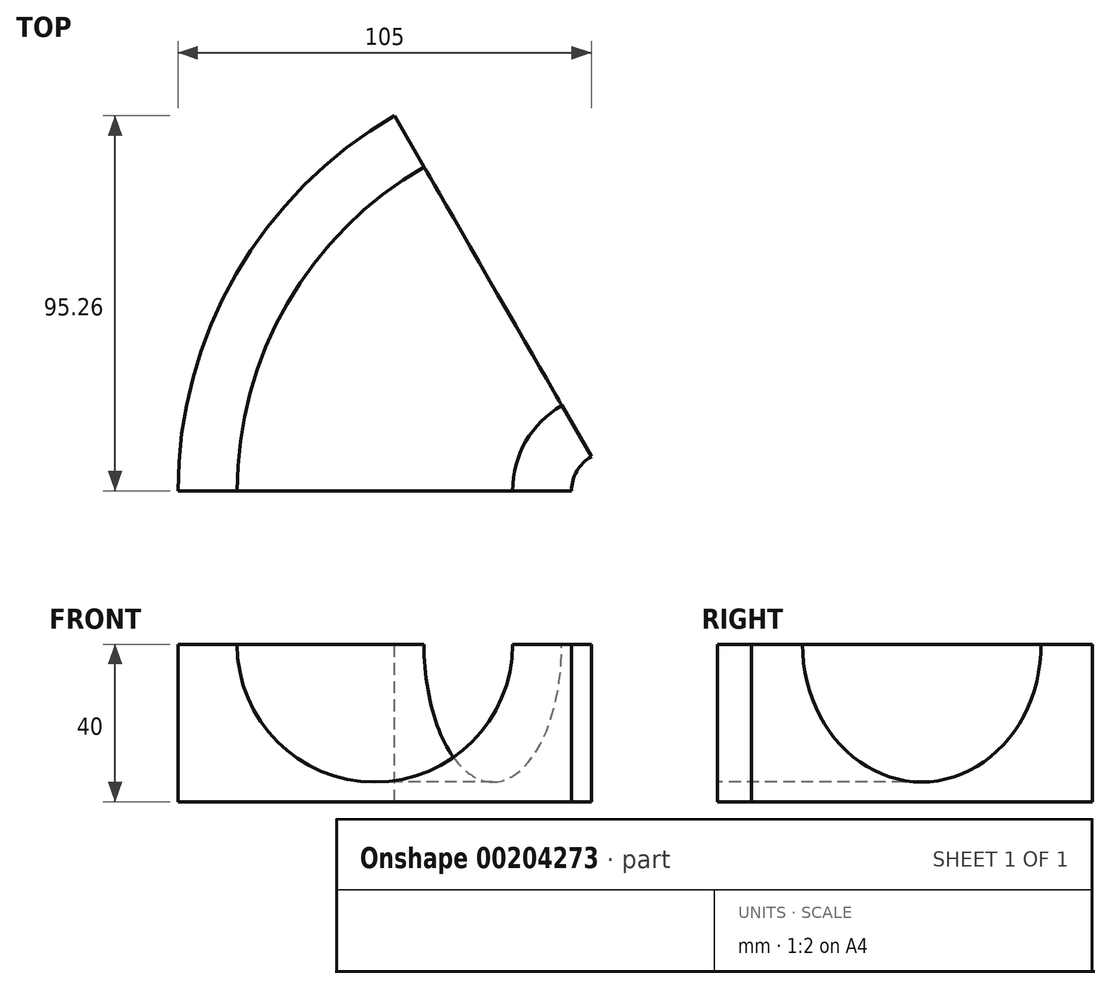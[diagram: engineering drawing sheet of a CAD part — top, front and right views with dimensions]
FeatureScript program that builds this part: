
annotation { "Feature Type Name" : "Feature", "Feature Type Description" : "" }
export const myFeature = defineFeature(function(context is Context, id is Id, definition is map)
    precondition{}
    {
        {
            var Q0;
            Q0=qCreatedBy(makeId("Front.planeOp"),FACE);
            var sketch = newSketch(context, id + "F0", { "sketchPlane" : qUnion([Q0])});
            skLineSegment(sketch, "E0.bottom", {"start": v(-50, -19.67) * mm, "end": v(0, -19.67) * mm});
            skLineSegment(sketch, "E0.top", {"start": v(-50, 20.33) * mm, "end": v(0, 20.33) * mm});
            skLineSegment(sketch, "E0.left", {"start": v(-50, -19.67) * mm, "end": v(-50, 20.33) * mm});
            skLineSegment(sketch, "E1.MirrorCS", {"start": v(50, -19.67) * mm, "end": v(0, -19.67) * mm});
            skLineSegment(sketch, "E2.MirrorCS", {"start": v(50, -19.67) * mm, "end": v(50, 20.33) * mm});
            skLineSegment(sketch, "E3.MirrorCS", {"start": v(50, 20.33) * mm, "end": v(0, 20.33) * mm});
            skArc(sketch, "E4", {"start": v(-35, 20.33) * mm, "mid": v(0, -14.67) * mm, "end": v(35, 20.33) * mm});
            skLineSegment(sketch, "E5", {"start": v(50, 20.33) * mm, "end": v(60, 20.33) * mm, "construction": true});
            skLineSegment(sketch, "E6", {"start": v(60, 20.33) * mm, "end": v(60, -18.07) * mm, "construction": true});
            skSolve(sketch);
        }
        {
            var Q0;
            Q0=makeQuery(id+"F0.imprint","IMPRINT",FACE,{"disambiguationData":[TD([[makeQuery(id+"F0.imprint","IMPRINT",EDGE,{"derivedFrom":sQuery(id+"F0.wireOp",EDGE,"E0.bottom")}),1.0]])]});
            var Q1;
            Q1=sQuery(id+"F0.wireOp",EDGE,"E6");
            revolve(context, id + "F1", {"entities" : qUnion([Q0]), "axis" : qUnion([Q1]), "revolveType" : RevolveType.ONE_DIRECTION, "angle" : 60 * degree});
        }
    });
